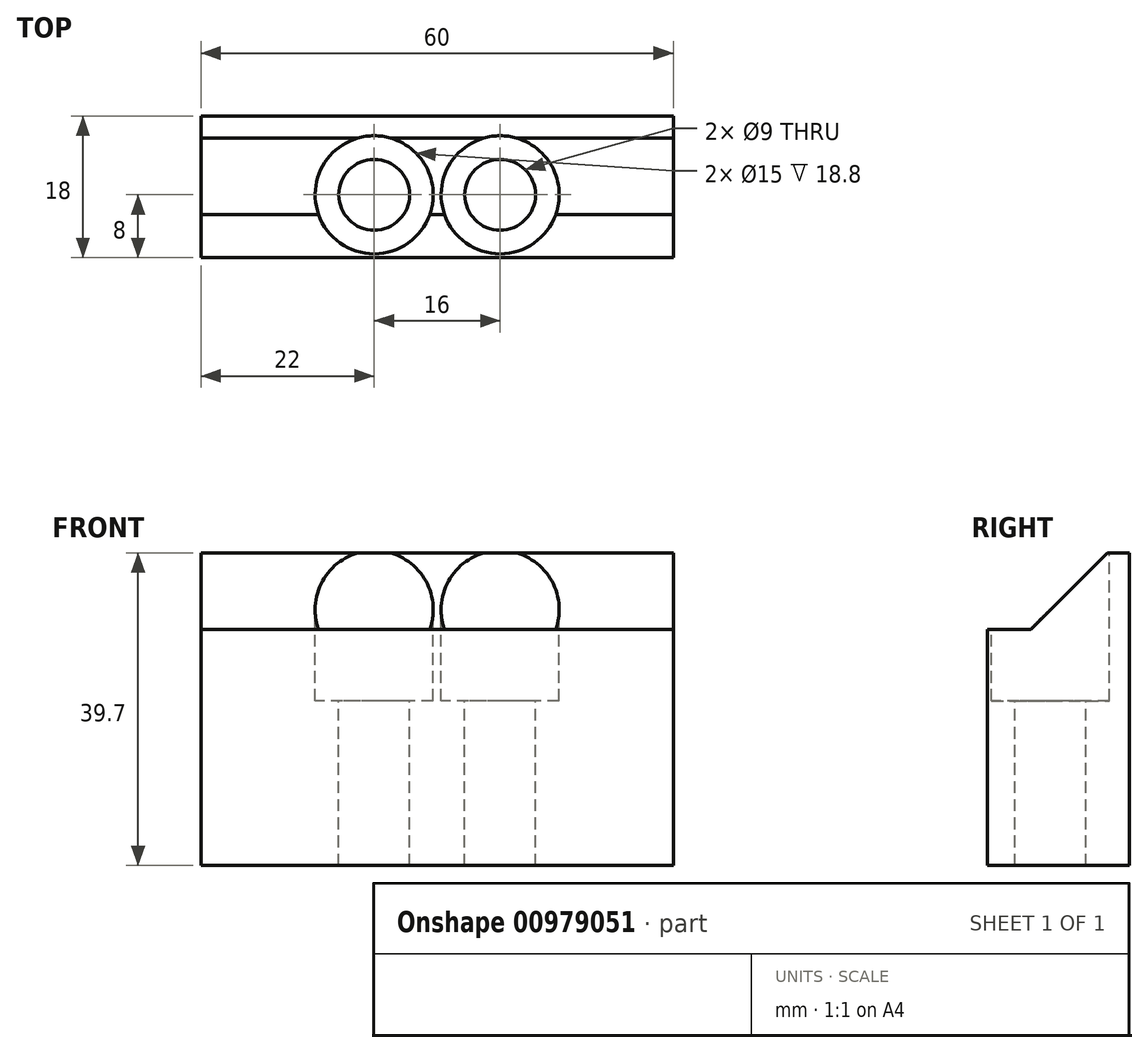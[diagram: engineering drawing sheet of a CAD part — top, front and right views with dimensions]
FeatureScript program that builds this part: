
annotation { "Feature Type Name" : "Feature", "Feature Type Description" : "" }
export const myFeature = defineFeature(function(context is Context, id is Id, definition is map)
    precondition{}
    {
        {
            var Q0;
            Q0=qCreatedBy(makeId("Right.planeOp"),FACE);
            var sketch = newSketch(context, id + "F0", { "sketchPlane" : qUnion([Q0])});
            skLineSegment(sketch, "E0", {"start": v(0, 0) * mm, "end": v(-18, 0) * mm});
            skLineSegment(sketch, "E1", {"start": v(-18, 0) * mm, "end": v(-18, 30) * mm});
            skLineSegment(sketch, "E2", {"start": v(-18, 30) * mm, "end": v(-12.5, 30) * mm});
            skLineSegment(sketch, "E3", {"start": v(-12.5, 30) * mm, "end": v(-2.8, 39.7) * mm});
            skLineSegment(sketch, "E4", {"start": v(-2.8, 39.7) * mm, "end": v(0, 39.7) * mm});
            skLineSegment(sketch, "E5", {"start": v(0, 39.7) * mm, "end": v(0, 0) * mm});
            skSolve(sketch);
        }
        {
            var Q0;
            Q0=makeQuery(id+"F0.imprint","IMPRINT",FACE,{"disambiguationData":[TD([[makeQuery(id+"F0.imprint","IMPRINT",EDGE,{"derivedFrom":sQuery(id+"F0.wireOp",EDGE,"E0")}),-1.0]])]});
            extrude(context, id + "F1", {"entities" : qUnion([Q0]), "endBound" : BoundingType.SYMMETRIC, "depth" : 60 * mm, "offsetDistance" : 25 * mm});
        }
        {
            var Q0;
            Q0=makeQuery(id+"F1.opExtrude","SWEPT_FACE",FACE,{"disambiguationData":[OSD([sQuery(id+"F0.wireOp",EDGE,"E4")])]});
            var sketch = newSketch(context, id + "F2", { "sketchPlane" : qUnion([Q0])});
            skPoint(sketch, "E6", {"position": v(-8, -10) * mm});
            skPoint(sketch, "E7", {"position": v(8, -10) * mm});
            skSolve(sketch);
        }
        {
            var Q0;
            Q0=sQuery(id+"F2.wireOp",VERTEX,"E6");
            var Q1;
            Q1=sQuery(id+"F2.wireOp",VERTEX,"E7");
            var Q2;
            Q2=makeQuery(id+"F1.opExtrude","SWEPT_BODY",BODY,{"disambiguationData":[OSD([sQuery(id+"F0.wireOp",EDGE,"E0"),sQuery(id+"F0.wireOp",EDGE,"E1"),sQuery(id+"F0.wireOp",EDGE,"E2"),sQuery(id+"F0.wireOp",EDGE,"E3"),sQuery(id+"F0.wireOp",EDGE,"E4"),sQuery(id+"F0.wireOp",EDGE,"E5")])]});
            hole(context, id + "F3", {"style" : HoleStyle.C_BORE, "endStyle" : HoleEndStyle.THROUGH, "holeDiameter" : 9 * mm, "cBoreDiameter" : 15 * mm, "cBoreDepth" : 18.8 * mm, "majorDiameter" : 5 * mm, "isTappedThrough" : true, "tappedDepth" : 12 * mm, "tapClearance" : 3, "startFromSketch" : true, "locations" : qUnion([Q0, Q1]), "scope" : qUnion([Q2])});
        }
    });
